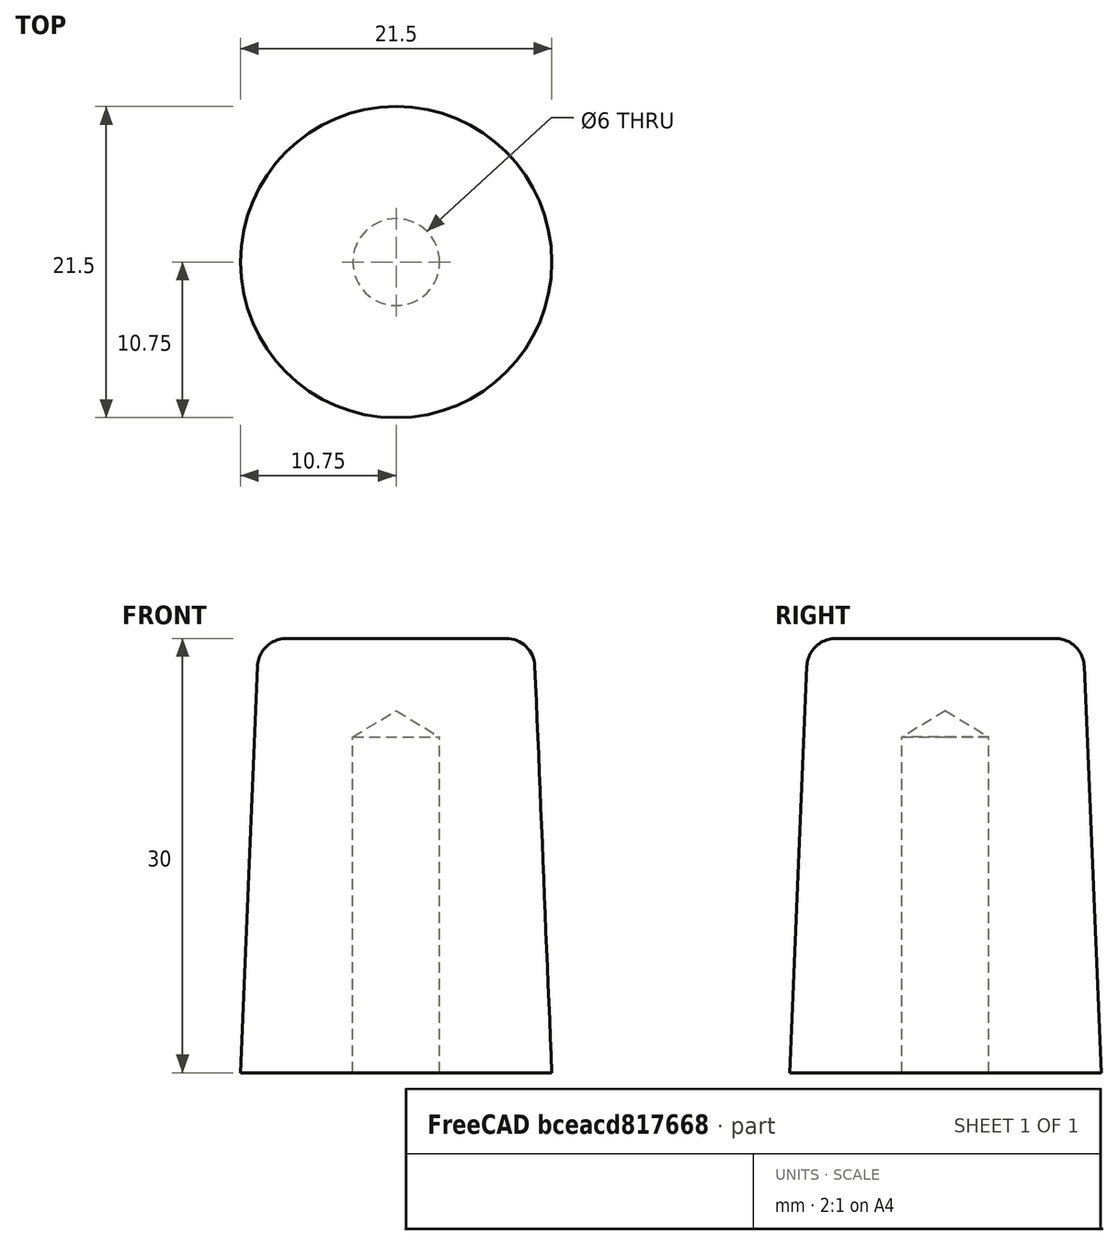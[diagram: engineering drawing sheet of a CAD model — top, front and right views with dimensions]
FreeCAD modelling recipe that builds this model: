
FCSTD DOCUMENT  (FreeCAD 0.18R16155 (Git))
Label: window_blocker
License: All rights reserved
LicenseURL: http://en.wikipedia.org/wiki/All_rights_reserved
objects: Sketcher::SketchObject×3, PartDesign::AdditiveLoft×1, PartDesign::Fillet×1, PartDesign::Hole×1, PartDesign::Body×1, App::Part×1
note: 9 computed .brp shape members not serialized (recipe doc carries the construction recipe); baked Part::Feature solids carry a one-line shape summary decoded from their .brp

FEATURE [Sketcher::SketchObject] Sketch
  MapMode = 5
  Support = -> [XY_Plane001]
  sketch-geometry (1):
    g0: Circle CenterX=0 CenterY=0 CenterZ=0 NormalX=0 NormalY=0 NormalZ=1 AngleXU=0 Radius=10.75
  constraints (1):
    c: Diameter(g0) = 21.5
FEATURE [Sketcher::SketchObject] Sketch001
  AttachmentOffset = pos=(0,0,30) rot=(0,0,1;0rad)
  MapMode = 5
  Placement = pos=(0,0,30) rot=(0,0,1;0rad)
  Support = -> [XY_Plane001]
  sketch-geometry (1):
    g0: Circle CenterX=0 CenterY=0 CenterZ=0 NormalX=0 NormalY=0 NormalZ=1 AngleXU=0 Radius=9.5
  constraints (1):
    c: Diameter(g0) = 19
FEATURE [PartDesign::AdditiveLoft] AdditiveLoft
  Closed = false
  Profile = -> Sketch
  Ruled = false
  Sections = -> [Sketch001]
FEATURE [PartDesign::Fillet] Fillet
  Base = -> AdditiveLoft [Edge3]
  BaseFeature = -> AdditiveLoft
  Radius = 2
FEATURE [Sketcher::SketchObject] Sketch002
  MapMode = 5
  Placement = pos=(0,0,0) rot=(1,0,0;3.14159rad)
  Support = -> [Fillet]
  sketch-geometry (1):
    g0: Circle CenterX=0 CenterY=0 CenterZ=0 NormalX=0 NormalY=0 NormalZ=1 AngleXU=0 Radius=2.9
  constraints (1):
    c: Diameter(g0) = 5.8
FEATURE [PartDesign::Hole] Hole
  BaseFeature = -> Fillet
  Depth = 15
  DepthType = 0
  Diameter = 6
  DrillPoint = 1
  DrillPointAngle = 118
  HoleCutCountersinkAngle = 90
  HoleCutDepth = 0
  HoleCutDiameter = 0
  HoleCutType = 0
  ModelActualThread = false
  Profile = -> Sketch002
  Tapered = false
  TaperedAngle = 90
  ThreadAngle = 0
  ThreadClass = 0
  ThreadCutOffInner = 0
  ThreadCutOffOuter = 0
  ThreadDirection = 0
  ThreadFit = 0
  ThreadPitch = 0
  ThreadSize = 0
  ThreadType = 0
  Threaded = false
FEATURE [PartDesign::Body] Body
  Group = -> [Sketch,Sketch001,AdditiveLoft,Fillet,Sketch002,Hole]
  Origin = -> Origin001
  Tip = -> Hole
FEATURE [App::Part] Part
  Group = -> [Body]
  Origin = -> Origin
